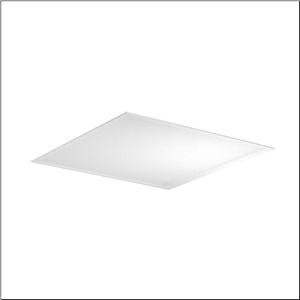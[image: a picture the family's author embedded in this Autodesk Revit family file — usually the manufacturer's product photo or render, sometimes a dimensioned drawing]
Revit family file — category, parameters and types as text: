
# Revit family: apollon_r__21_square_51mq12wd2t13_0a2d
name_source: partatom
category: Lighting Fixtures
units: mm (PartAtom-declared; Revit-internal decimal feet)

## family parameters
Cut with Voids When Loaded = No
Host = Face
Light Source = No
Part Type = Normal
Room Calculation Point = No
Round Connector Dimension = Use Diameter
Shared = No

## types (1)
- --- (1 x LED 2700 K ... 6500 K, 4000 lm, 40 W, 2700K)
    Apparent Load = 40 VA
    CIE Flux Codes = 61 87 97 100 100
    Color Rendering = 80
    Color Temperature = 2700K
    Default Elevation = 1800 mm
    Description = Apollon® 21 square, office luminaire, primary optical cover: micro prismatic cover, of PMMA, CAT 2 (L<= 3000cd/m²), light emission: direct distribution, primary light characteristic: symmetric, installation type: lay-in mounting, LED, rated luminous flux: 4.000lm, luminous efficacy: 100lm/W, light colour: 8tw, colour temperature: 2700..6500K, control gear: ECG DALI, with terminal, 5-pole, mains connection: 220..240V, AC, 50/60Hz, rated input power: 40W, housing, of aluminium, traffic white (RAL 9016), module: M600, length: 596mm, width: 596mm, height: 40mm, housing upper side, of sheet steel, galvanised, protection rating (complete): IP20, protection rating (lamp compartment, on room side): IP50, insulation class (complete): insulation class I (protective earthing), certification: CE, ENEC, permissible operating ambient temperature: -20..+40°C, packaging unit: 1 piece
    Height = 0 mm  [stored 0 ft]
    Lamp = 1 x LED 2700 K ... 6500 K
    Lamp Light Flux = 4000 lm
    Lamp Power = 40 W
    Lamp count = 1
    Length = 595 mm
    Luminous efficacy = 100 lm/W
    Manufacturer = Siteco
    ModVariant = No
    Model = 51MQ12WD2T13
    Mounting Place = Ceiling
    Mounting Type = Recessed
    Number of Poles = 1
    OnlyDefault = Yes
    Power Factor = 1
    Product Name = Apollon® 21 square
    Product group = office luminaire | ceiling recessed
    ProductGroupID = 401
    Protection Class = Protection class I
    Protection Degree = IP 20
    RLX_Detail_Level = 1
    RLX_Emergency_Light_Flux = 0 lm
    RLX_Emergency_Type = 0
    RLX_Emergency_Type_DB = No
    RlxData = <blob elided: 14705 chars, md5=1f94faf0>
    Socket = socket
    Standby Power = 0 W
    System Light Flux = 4000 lm
    System Power = 40 W
    Type Comments = individual setting: CCT=2700K
    Type Image = l_1291049.jpg
    URL = http://relux.com
    VarID = @adj_050601
    Voltage = 0 V
    Weight = 0.00 kg
    Width = 595 mm

note: [stored X ft] marks values corroborated as IEEE doubles in the binary element streams (Revit-internal decimal feet)

## geometry (parser evidence)
native form markers: Sweep x12
no freeform markers — native parametric forms only
